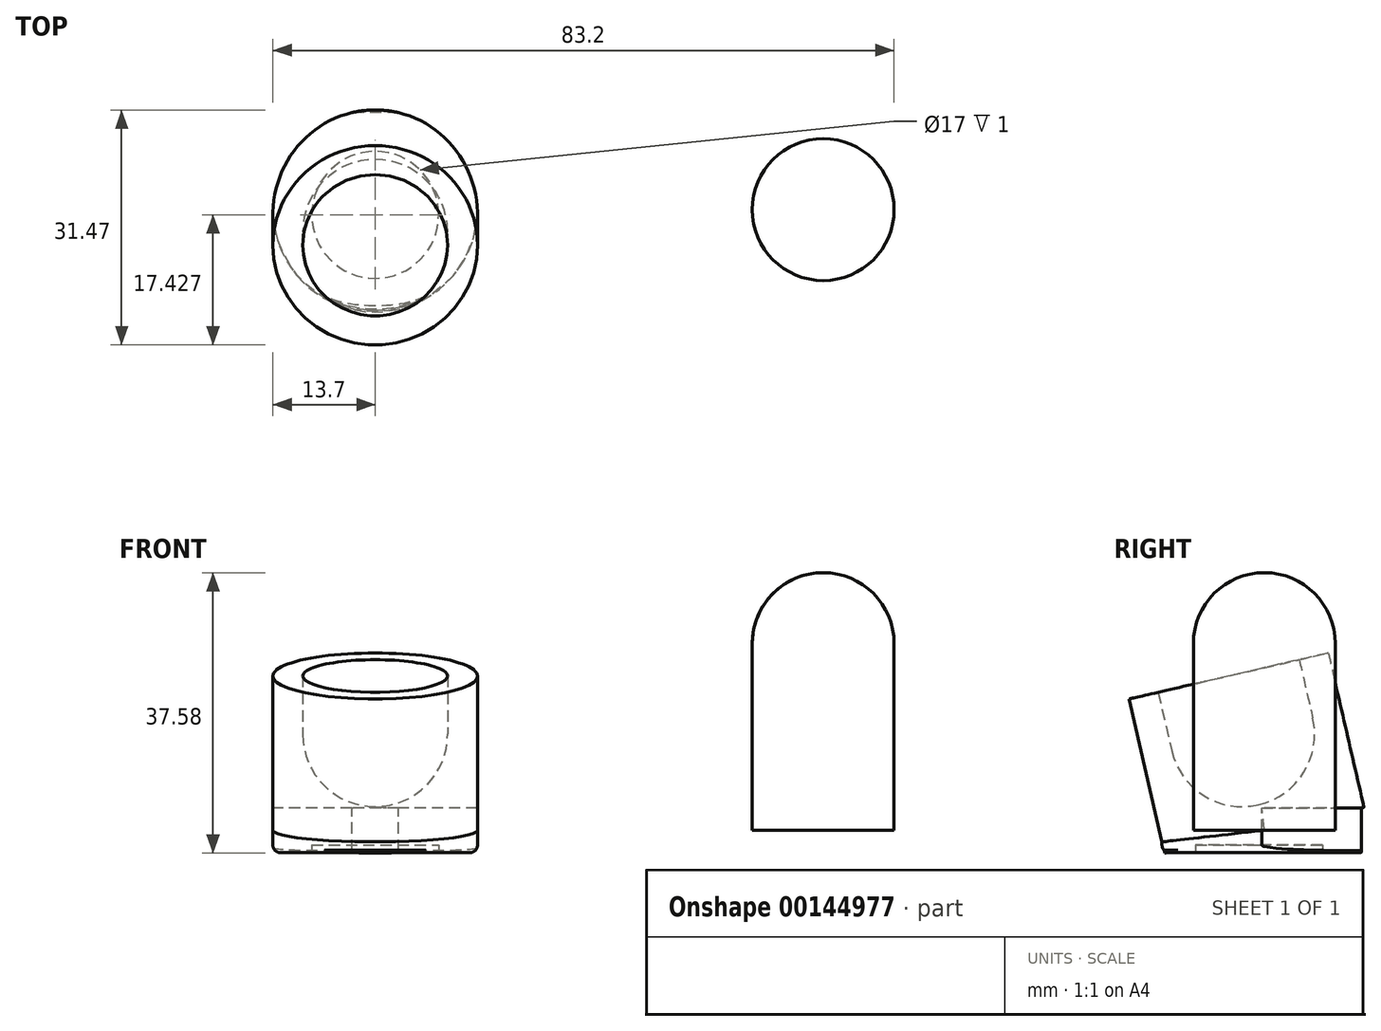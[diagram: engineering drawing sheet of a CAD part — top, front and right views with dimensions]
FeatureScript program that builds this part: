
annotation { "Feature Type Name" : "Feature", "Feature Type Description" : "" }
export const myFeature = defineFeature(function(context is Context, id is Id, definition is map)
    precondition{}
    {
        {
            var Q0;
            Q0=qCreatedBy(makeId("Top.planeOp"),FACE);
            var sketch = newSketch(context, id + "F0", { "sketchPlane" : qUnion([Q0])});
            skCircle(sketch, "E0", {"center": v(0, 0) * mm, "radius": 9.7 * mm});
            skCircle(sketch, "E1", {"center": v(0, 0) * mm, "radius": 13.7 * mm});
            skSolve(sketch);
        }
        {
            var Q0;
            Q0=qCreatedBy(makeId("Front.planeOp"),FACE);
            var sketch = newSketch(context, id + "F1", { "sketchPlane" : qUnion([Q0])});
            skLineSegment(sketch, "E2", {"start": v(0, 0) * mm, "end": v(0, 25.1) * mm});
            skLineSegment(sketch, "E3", {"start": v(-29.22, 0) * mm, "end": v(33.24, 0) * mm});
            skSolve(sketch);
        }
        {
            var Q0;
            Q0=sQuery(id+"F1.wireOp",EDGE,"E3");
            var Q1;
            Q1=sQuery(id+"F1.wireOp",EDGE,"E2");
            cPlane(context, id + "F2", {"entities" : qUnion([Q0, Q1]), "cplaneType" : CPlaneType.LINE_ANGLE, "offset" : 25 * mm, "angle" : 13 * degree, "width" : 150 * mm, "height" : 150 * mm});
        }
        {
            var Q0;
            Q0=qCreatedBy(id+"F2.planeOp",FACE);
            var sketch = newSketch(context, id + "F3", { "sketchPlane" : qUnion([Q0])});
            skLineSegment(sketch, "E4", {"start": v(0, 0) * mm, "end": v(0, 32.71) * mm, "construction": true});
            skLineSegment(sketch, "E5", {"start": v(0, 0) * mm, "end": v(0, 3.5) * mm});
            skLineSegment(sketch, "E6", {"start": v(9.7, 13.2) * mm, "end": v(9.7, 21.2) * mm});
            skLineSegment(sketch, "E7", {"start": v(13.7, 21.2) * mm, "end": v(13.7, 0) * mm});
            skLineSegment(sketch, "E8", {"start": v(13.7, 0) * mm, "end": v(0, 0) * mm});
            skLineSegment(sketch, "E9", {"start": v(9.7, 21.2) * mm, "end": v(13.7, 21.2) * mm});
            skArc(sketch, "E10", {"start": v(0, 3.5) * mm, "mid": v(6.86, 6.34) * mm, "end": v(9.7, 13.2) * mm});
            skSolve(sketch);
        }
        {
            var Q0;
            Q0 = qSketchRegion(id + "F3", true);
            var Q1;
            Q1=sQuery(id+"F3.wireOp",EDGE,"E4");
            revolve(context, id + "F4", {"entities" : qUnion([Q0]), "axis" : qUnion([Q1]), "revolveType" : RevolveType.FULL});
        }
        {
            var Q0;
            Q0=makeQuery(id+"F0.imprint","IMPRINT",FACE,{"disambiguationData":[TD([[makeQuery(id+"F0.imprint","IMPRINT",EDGE,{"derivedFrom":sQuery(id+"F0.wireOp",EDGE,"E0")}),-1.0]])]});
            var Q1;
            Q1=makeQuery(id+"F0.imprint","IMPRINT",FACE,{"disambiguationData":[TD([[makeQuery(id+"F0.imprint","IMPRINT",EDGE,{"derivedFrom":sQuery(id+"F0.wireOp",EDGE,"E0")}),1.0]])]});
            var Q2;
            Q2=makeQuery(id+"F4.opRevolve","SWEPT_FACE",FACE,{"disambiguationData":[OSD([sQuery(id+"F3.wireOp",EDGE,"E8")])]});
            extrude(context, id + "F5", {"entities" : qUnion([Q0, Q1]), "operationType" : NewBodyOperationType.ADD, "depth" : 3 * mm, "hasSecondDirection" : true, "secondDirectionOppositeDirection" : true, "secondDirectionBoundEntityFace" : qUnion([Q2]), "secondDirectionDepth" : 3 * mm});
        }
        {
            var Q0;
            Q0=makeQuery(id+"F5.opExtrude","CAP_FACE",FACE,{"disambiguationData":[OSD([sQuery(id+"F0.wireOp",EDGE,"E1")])],"isStart":false});
            var Q1;
            Q1=makeQuery(id+"F5.opExtrude","CAP_FACE",FACE,{"disambiguationData":[OSD([sQuery(id+"F0.wireOp",EDGE,"E1")])],"isStart":true});
            extrude(context, id + "F6", {"entities" : qUnion([Q0]), "operationType" : NewBodyOperationType.REMOVE, "endBound" : BoundingType.UP_TO_SURFACE, "oppositeDirection" : true, "endBoundEntityFace" : qUnion([Q1]), "depth" : 25 * mm});
        }
        {
            var Q0;
            Q0=makeQuery(id+"F5.opExtrude","CAP_FACE",FACE,{"disambiguationData":[OSD([sQuery(id+"F0.wireOp",EDGE,"E1")])],"isStart":true});
            var sketch = newSketch(context, id + "F7", { "sketchPlane" : qUnion([Q0])});
            skCircle(sketch, "E11", {"center": v(0, 0.7) * mm, "radius": 8.5 * mm});
            skSolve(sketch);
        }
        {
            var Q0;
            Q0 = qSketchRegion(id + "F7", true);
            extrude(context, id + "F8", {"entities" : qUnion([Q0]), "operationType" : NewBodyOperationType.REMOVE, "oppositeDirection" : true, "depth" : 1 * mm});
        }
        {
            var Q0;
            Q0=makeQuery(id+"F5.opExtrude","CAP_EDGE",EDGE,{"disambiguationData":[OSD([sQuery(id+"F0.wireOp",EDGE,"E1")])],"isStart":true});
            var Q1;
            {var subQ0=sQuery(id+"F0.wireOp",EDGE,"E1");var subQ1=makeQuery(id+"F5.opExtrude","CAP_FACE",FACE,{"disambiguationData":[OSD([subQ0])],"isStart":false});var subQ2=sQuery(id+"F3.wireOp",EDGE,"E7");var subQ3=makeQuery(id+"F4.opRevolve","SWEPT_FACE",FACE,{"disambiguationData":[OSD([subQ2])]});Q1=qUnion([makeQuery(id+"F6.boolean.opBoolean","COPY",EDGE,{"derivedFrom":makeQuery(id+"F6.opExtrude","CAP_EDGE",EDGE,{"disambiguationData":[OSD([subQ0,subQ2]),TDD([makeQuery(id+"F5.boolean.opBoolean","INTERSECT",EDGE,{"disambiguationData":[OD(0.0)],"derivedFrom":[subQ3,subQ1]})])],"isStart":false})}),makeQuery(id+"F6.boolean.opBoolean","COPY",EDGE,{"derivedFrom":makeQuery(id+"F6.opExtrude","CAP_EDGE",EDGE,{"disambiguationData":[OSD([subQ0,subQ2]),TDD([makeQuery(id+"F5.boolean.opBoolean","INTERSECT",EDGE,{"disambiguationData":[OD(1.0)],"derivedFrom":[subQ3,subQ1]})])],"isStart":false})})]);}
            fillet(context, id + "F9", {"entities" : qUnion([Q0, Q1]), "radius" : 1 * mm, "tangentPropagation" : true, "allowEdgeOverflow" : false});
        }
        {
            var Q0;
            Q0=qCreatedBy(makeId("Top.planeOp"),FACE);
            var sketch = newSketch(context, id + "F10", { "sketchPlane" : qUnion([Q0])});
            skCircle(sketch, "E12", {"center": v(60, 0) * mm, "radius": 9.5 * mm});
            skSolve(sketch);
        }
        {
            var Q0;
            Q0 = qSketchRegion(id + "F10", true);
            extrude(context, id + "F11", {"entities" : qUnion([Q0]), "depth" : 25 * mm});
        }
        {
            var Q0;
            Q0=qCreatedBy(makeId("Front.planeOp"),FACE);
            var sketch = newSketch(context, id + "F12", { "sketchPlane" : qUnion([Q0])});
            skLineSegment(sketch, "E13", {"start": v(60, 25) * mm, "end": v(50.5, 25) * mm});
            skLineSegment(sketch, "E14", {"start": v(60, 25) * mm, "end": v(60, 34.5) * mm});
            skArc(sketch, "E15", {"start": v(60, 34.5) * mm, "mid": v(53.28, 31.72) * mm, "end": v(50.5, 25) * mm});
            skSolve(sketch);
        }
        {
            var Q0;
            Q0 = qSketchRegion(id + "F12", true);
            var Q1;
            Q1=makeQuery(id+"F11.opExtrude","CAP_EDGE",EDGE,{"disambiguationData":[OSD([sQuery(id+"F10.wireOp",EDGE,"E12")])],"isStart":false});
            revolve(context, id + "F13", {"operationType" : NewBodyOperationType.ADD, "entities" : qUnion([Q0]), "axis" : qUnion([Q1]), "revolveType" : RevolveType.FULL});
        }
    });
